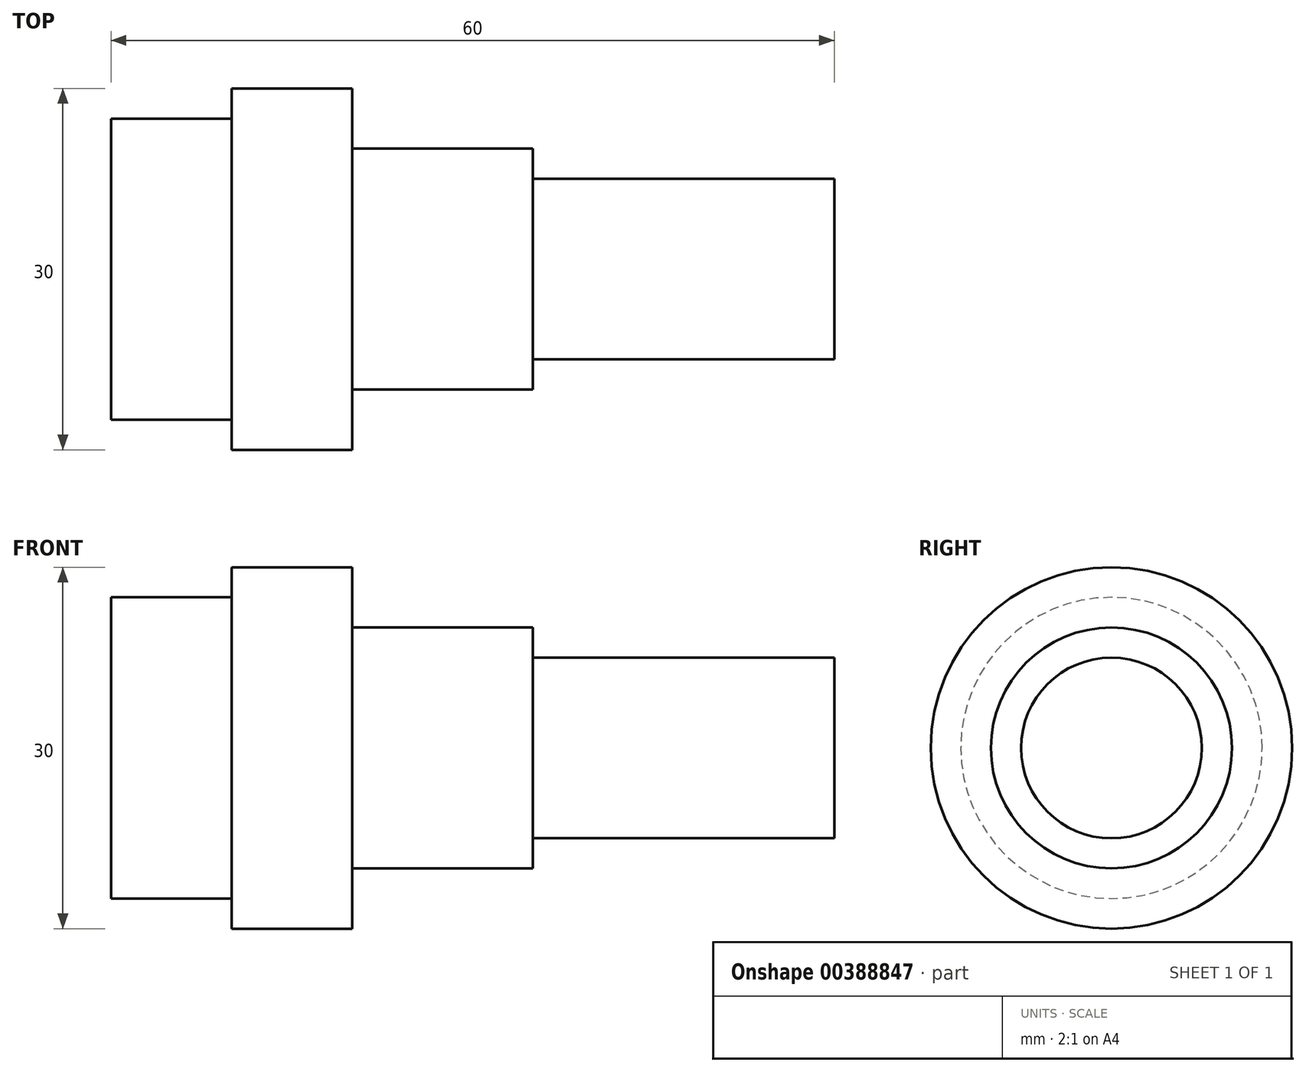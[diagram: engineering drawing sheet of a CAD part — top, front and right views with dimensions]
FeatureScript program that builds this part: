
annotation { "Feature Type Name" : "Feature", "Feature Type Description" : "" }
export const myFeature = defineFeature(function(context is Context, id is Id, definition is map)
    precondition{}
    {
        {
            var Q0;
            Q0=qCreatedBy(makeId("Front.planeOp"),FACE);
            var sketch = newSketch(context, id + "F0", { "sketchPlane" : qUnion([Q0])});
            skLineSegment(sketch, "E0", {"start": v(0, 0) * mm, "end": v(0, 7.5) * mm});
            skLineSegment(sketch, "E1", {"start": v(0, 7.5) * mm, "end": v(-25, 7.5) * mm});
            skLineSegment(sketch, "E2", {"start": v(-25, 7.5) * mm, "end": v(-25, 10) * mm});
            skLineSegment(sketch, "E3", {"start": v(-25, 10) * mm, "end": v(-40, 10) * mm});
            skLineSegment(sketch, "E4", {"start": v(-40, 10) * mm, "end": v(-40, 15) * mm});
            skLineSegment(sketch, "E5", {"start": v(-40, 15) * mm, "end": v(-50, 15) * mm});
            skLineSegment(sketch, "E6", {"start": v(-50, 15) * mm, "end": v(-50, 12.5) * mm});
            skLineSegment(sketch, "E7", {"start": v(-50, 12.5) * mm, "end": v(-60, 12.5) * mm});
            skLineSegment(sketch, "E8", {"start": v(-60, 12.5) * mm, "end": v(-60, 0) * mm});
            skLineSegment(sketch, "E9", {"start": v(-60, 0) * mm, "end": v(0, 0) * mm});
            skLineSegment(sketch, "E10", {"start": v(-99.68, 0) * mm, "end": v(44.94, 0) * mm, "construction": true});
            skSolve(sketch);
        }
        {
            var Q0;
            Q0=makeQuery(id+"F0.imprint","IMPRINT",FACE,{"disambiguationData":[TD([[makeQuery(id+"F0.imprint","IMPRINT",EDGE,{"derivedFrom":sQuery(id+"F0.wireOp",EDGE,"E0")}),1.0]])]});
            var Q1;
            Q1=sQuery(id+"F0.wireOp",EDGE,"E10");
            revolve(context, id + "F1", {"entities" : qUnion([Q0]), "axis" : qUnion([Q1]), "revolveType" : RevolveType.FULL});
        }
    });
